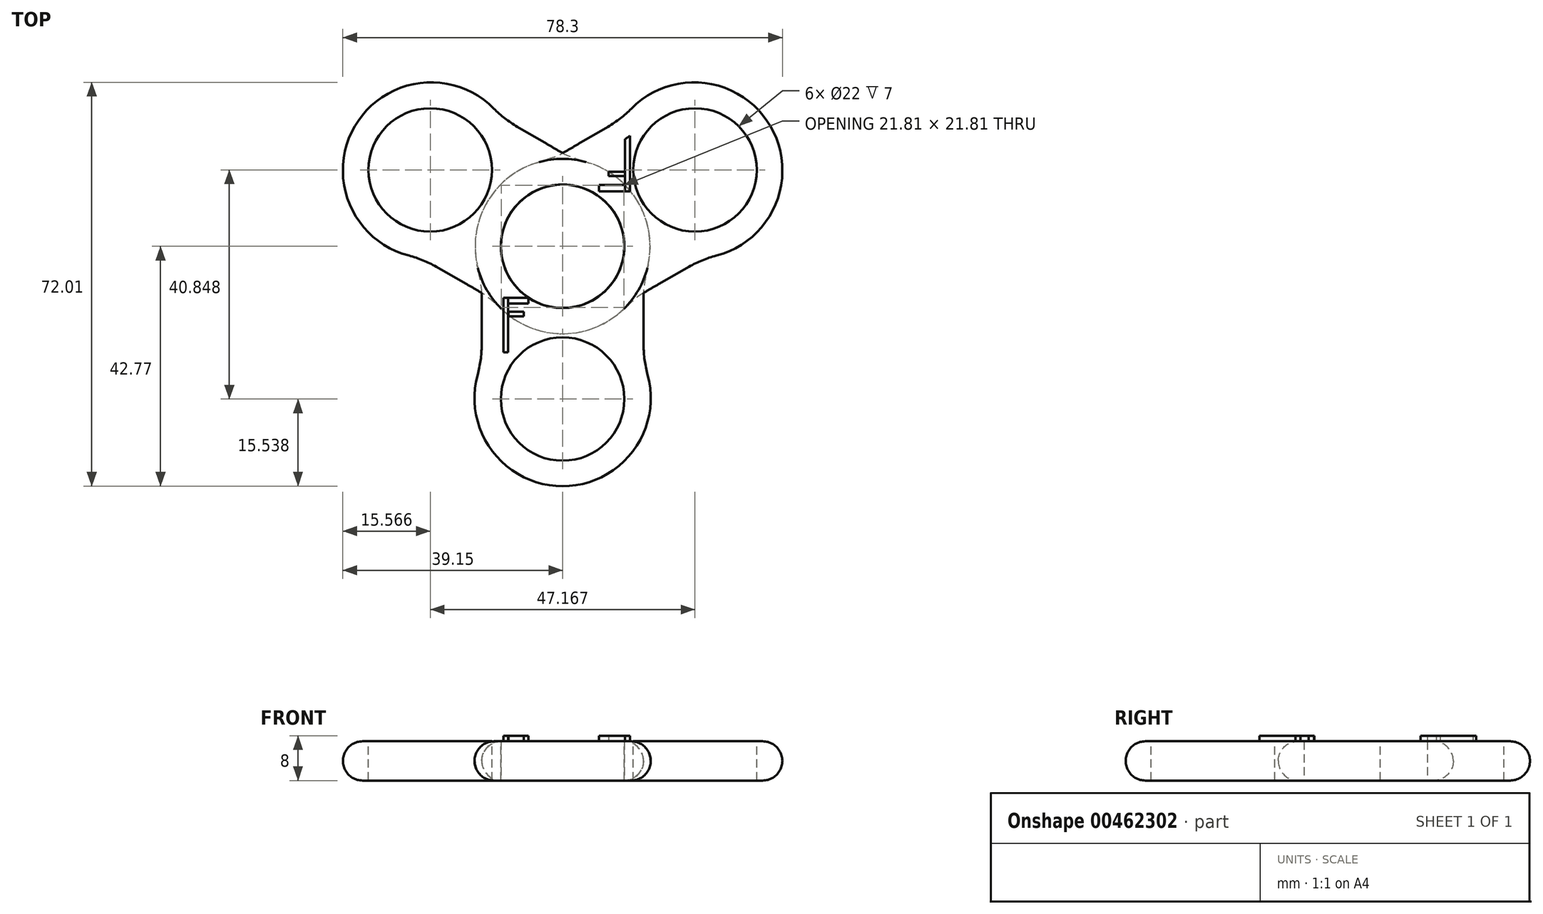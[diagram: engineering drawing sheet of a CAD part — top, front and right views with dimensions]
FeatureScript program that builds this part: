
annotation { "Feature Type Name" : "Feature", "Feature Type Description" : "" }
export const myFeature = defineFeature(function(context is Context, id is Id, definition is map)
    precondition{}
    {
        {
            var Q0;
            Q0=qCreatedBy(makeId("Top.planeOp"),FACE);
            var sketch = newSketch(context, id + "F0", { "sketchPlane" : qUnion([Q0])});
            skCircle(sketch, "E0", {"center": v(0, 0) * mm, "radius": 12.05 * mm});
            skSolve(sketch);
        }
        {
            var Q0;
            Q0=qCreatedBy(makeId("Top.planeOp"),FACE);
            var sketch = newSketch(context, id + "F1", { "sketchPlane" : qUnion([Q0])});
            skCircle(sketch, "E1", {"center": v(0, 0) * mm, "radius": 15.6 * mm});
            skSolve(sketch);
        }
        {
            var Q0;
            Q0=makeQuery(id+"F1.imprint","IMPRINT",FACE,{"disambiguationData":[TD([[makeQuery(id+"F1.imprint","IMPRINT",EDGE,{"derivedFrom":sQuery(id+"F1.wireOp",EDGE,"E1")}),1.0]])]});
            extrude(context, id + "F2", {"entities" : qUnion([Q0]), "depth" : 7 * mm, "offsetDistance" : 25 * mm});
        }
        {
            var Q0;
            Q0=sQuery(id+"F0.wireOp",VERTEX,"E0.center");
            var Q1;
            Q1=makeQuery(id+"F2.opExtrude","SWEPT_BODY",BODY,{"disambiguationData":[OSD([sQuery(id+"F1.wireOp",EDGE,"E1")])]});
            hole(context, id + "F3", {"style" : HoleStyle.SIMPLE, "endStyle" : HoleEndStyle.THROUGH, "oppositeDirection" : true, "holeDiameter" : 22 * mm, "majorDiameter" : 5 * mm, "isTappedThrough" : true, "tappedDepth" : 12 * mm, "tapClearance" : 3, "locations" : qUnion([Q0]), "scope" : qUnion([Q1])});
        }
        {
            var Q0;
            Q0=qCreatedBy(makeId("Top.planeOp"),FACE);
            var sketch = newSketch(context, id + "F4", { "sketchPlane" : qUnion([Q0])});
            skCircle(sketch, "E2", {"center": v(0, -27.23) * mm, "radius": 14.56 * mm});
            skSolve(sketch);
        }
        {
            var Q0;
            Q0=makeQuery(id+"F4.imprint","IMPRINT",FACE,{"disambiguationData":[TD([[makeQuery(id+"F4.imprint","IMPRINT",EDGE,{"derivedFrom":sQuery(id+"F4.wireOp",EDGE,"E2")}),1.0]])]});
            extrude(context, id + "F5", {"entities" : qUnion([Q0]), "operationType" : NewBodyOperationType.ADD, "depth" : 7 * mm, "offsetDistance" : 25 * mm});
        }
        {
            var Q0;
            Q0=makeQuery(id+"F5.boolean.opBoolean","MERGE",FACE,{"derivedFrom":[makeQuery(id+"F2.opExtrude","CAP_FACE",FACE,{"disambiguationData":[OSD([sQuery(id+"F1.wireOp",EDGE,"E1")])],"isStart":false}),makeQuery(id+"F5.opExtrude","CAP_FACE",FACE,{"disambiguationData":[OSD([sQuery(id+"F4.wireOp",EDGE,"E2")])],"isStart":false})]});
            var sketch = newSketch(context, id + "F6", { "sketchPlane" : qUnion([Q0])});
            skCircle(sketch, "E3", {"center": v(0, -27.23) * mm, "radius": 12.26 * mm});
            skSolve(sketch);
        }
        {
            var Q0;
            Q0=qCreatedBy(makeId("Top.planeOp"),FACE);
            var sketch = newSketch(context, id + "F7", { "sketchPlane" : qUnion([Q0])});
            skCircle(sketch, "E4", {"center": v(0, -27.07) * mm, "radius": 15.7 * mm});
            skSolve(sketch);
        }
        {
            var Q0;
            Q0=makeQuery(id+"F7.imprint","IMPRINT",FACE,{"disambiguationData":[TD([[makeQuery(id+"F7.imprint","IMPRINT",EDGE,{"derivedFrom":sQuery(id+"F7.wireOp",EDGE,"E4")}),1.0]])]});
            extrude(context, id + "F8", {"entities" : qUnion([Q0]), "operationType" : NewBodyOperationType.ADD, "depth" : 7 * mm, "offsetDistance" : 25 * mm});
        }
        {
            var Q0;
            Q0=sQuery(id+"F6.wireOp",VERTEX,"E3.center");
            var Q1;
            Q1=makeQuery(id+"F2.opExtrude","SWEPT_BODY",BODY,{"disambiguationData":[OSD([sQuery(id+"F1.wireOp",EDGE,"E1")])]});
            hole(context, id + "F9", {"style" : HoleStyle.SIMPLE, "endStyle" : HoleEndStyle.THROUGH, "holeDiameter" : 22 * mm, "majorDiameter" : 5 * mm, "isTappedThrough" : true, "tappedDepth" : 12 * mm, "tapClearance" : 3, "locations" : qUnion([Q0]), "scope" : qUnion([Q1])});
        }
        {
            var Q0;
            Q0=makeQuery(id+"F2.opExtrude","SWEPT_BODY",BODY,{"disambiguationData":[OSD([sQuery(id+"F1.wireOp",EDGE,"E1")])]});
            var Q1;
            Q1=makeQuery(id+"F2.opExtrude","SWEPT_FACE",FACE,{"disambiguationData":[OSD([sQuery(id+"F1.wireOp",EDGE,"E1")])]});
            circularPattern(context, id + "F10", {"entities" : qUnion([Q0]), "axis" : qUnion([Q1]), "angle" : 360 * degree, "instanceCount" : 3, "equalSpace" : true});
        }
        {
            var Q0;
            Q0=makeQuery(id+"F10.opPattern","COPY",EDGE,{"derivedFrom":makeQuery(id+"F8.boolean.opBoolean","INTERSECT",EDGE,{"disambiguationData":[OD(0.0)],"derivedFrom":[makeQuery(id+"F2.opExtrude","SWEPT_FACE",FACE,{"disambiguationData":[OSD([sQuery(id+"F1.wireOp",EDGE,"E1")])]}),makeQuery(id+"F8.opExtrude","SWEPT_FACE",FACE,{"disambiguationData":[OSD([sQuery(id+"F7.wireOp",EDGE,"E4")])]})]}),"instanceName":"2"});
            var Q1;
            Q1=makeQuery(id+"F8.boolean.opBoolean","INTERSECT",EDGE,{"disambiguationData":[OD(1.0)],"derivedFrom":[makeQuery(id+"F2.opExtrude","SWEPT_FACE",FACE,{"disambiguationData":[OSD([sQuery(id+"F1.wireOp",EDGE,"E1")])]}),makeQuery(id+"F8.opExtrude","SWEPT_FACE",FACE,{"disambiguationData":[OSD([sQuery(id+"F7.wireOp",EDGE,"E4")])]})]});
            var Q2;
            Q2=makeQuery(id+"F8.boolean.opBoolean","INTERSECT",EDGE,{"disambiguationData":[OD(0.0)],"derivedFrom":[makeQuery(id+"F2.opExtrude","SWEPT_FACE",FACE,{"disambiguationData":[OSD([sQuery(id+"F1.wireOp",EDGE,"E1")])]}),makeQuery(id+"F8.opExtrude","SWEPT_FACE",FACE,{"disambiguationData":[OSD([sQuery(id+"F7.wireOp",EDGE,"E4")])]})]});
            var Q3;
            Q3=makeQuery(id+"F10.opPattern","COPY",EDGE,{"derivedFrom":makeQuery(id+"F8.boolean.opBoolean","INTERSECT",EDGE,{"disambiguationData":[OD(1.0)],"derivedFrom":[makeQuery(id+"F2.opExtrude","SWEPT_FACE",FACE,{"disambiguationData":[OSD([sQuery(id+"F1.wireOp",EDGE,"E1")])]}),makeQuery(id+"F8.opExtrude","SWEPT_FACE",FACE,{"disambiguationData":[OSD([sQuery(id+"F7.wireOp",EDGE,"E4")])]})]}),"instanceName":"1"});
            var Q4;
            Q4=makeQuery(id+"F10.opPattern","COPY",EDGE,{"derivedFrom":makeQuery(id+"F8.boolean.opBoolean","INTERSECT",EDGE,{"disambiguationData":[OD(0.0)],"derivedFrom":[makeQuery(id+"F2.opExtrude","SWEPT_FACE",FACE,{"disambiguationData":[OSD([sQuery(id+"F1.wireOp",EDGE,"E1")])]}),makeQuery(id+"F8.opExtrude","SWEPT_FACE",FACE,{"disambiguationData":[OSD([sQuery(id+"F7.wireOp",EDGE,"E4")])]})]}),"instanceName":"1"});
            var Q5;
            Q5=makeQuery(id+"F10.opPattern","COPY",EDGE,{"derivedFrom":makeQuery(id+"F8.boolean.opBoolean","INTERSECT",EDGE,{"disambiguationData":[OD(1.0)],"derivedFrom":[makeQuery(id+"F2.opExtrude","SWEPT_FACE",FACE,{"disambiguationData":[OSD([sQuery(id+"F1.wireOp",EDGE,"E1")])]}),makeQuery(id+"F8.opExtrude","SWEPT_FACE",FACE,{"disambiguationData":[OSD([sQuery(id+"F7.wireOp",EDGE,"E4")])]})]}),"instanceName":"2"});
            chamfer(context, id + "F11", {"entities" : qUnion([Q0, Q1, Q2, Q3, Q4, Q5]), "width" : 19 * mm, "tangentPropagation" : true});
        }
        {
            var Q0;
            {var subQ0=makeQuery(id+"F2.opExtrude","SWEPT_FACE",FACE,{"disambiguationData":[OSD([sQuery(id+"F1.wireOp",EDGE,"E1")])]});Q0=makeQuery(id+"F11.opChamfer","BLEND_EDGE",EDGE,{"blendedFrom":[makeQuery(id+"F8.boolean.opBoolean","INTERSECT",EDGE,{"disambiguationData":[OD(1.0)],"derivedFrom":[subQ0,makeQuery(id+"F8.opExtrude","SWEPT_FACE",FACE,{"disambiguationData":[OSD([sQuery(id+"F7.wireOp",EDGE,"E4")])]})]}),subQ0],"blendedInto":[subQ0]});}
            var Q1;
            {var subQ0=makeQuery(id+"F2.opExtrude","SWEPT_FACE",FACE,{"disambiguationData":[OSD([sQuery(id+"F1.wireOp",EDGE,"E1")])]});Q1=makeQuery(id+"F11.opChamfer","BLEND_EDGE",EDGE,{"blendedFrom":[makeQuery(id+"F10.opPattern","COPY",EDGE,{"derivedFrom":makeQuery(id+"F8.boolean.opBoolean","INTERSECT",EDGE,{"disambiguationData":[OD(0.0)],"derivedFrom":[subQ0,makeQuery(id+"F8.opExtrude","SWEPT_FACE",FACE,{"disambiguationData":[OSD([sQuery(id+"F7.wireOp",EDGE,"E4")])]})]}),"instanceName":"2"}),makeQuery(id+"F10.opPattern","COPY",FACE,{"derivedFrom":subQ0,"instanceName":"2"})],"blendedInto":[makeQuery(id+"F10.opPattern","COPY",FACE,{"derivedFrom":subQ0,"instanceName":"2"})]});}
            var Q2;
            {var subQ0=makeQuery(id+"F2.opExtrude","SWEPT_FACE",FACE,{"disambiguationData":[OSD([sQuery(id+"F1.wireOp",EDGE,"E1")])]});Q2=makeQuery(id+"F11.opChamfer","BLEND_EDGE",EDGE,{"blendedFrom":[makeQuery(id+"F10.opPattern","COPY",EDGE,{"derivedFrom":makeQuery(id+"F8.boolean.opBoolean","INTERSECT",EDGE,{"disambiguationData":[OD(1.0)],"derivedFrom":[subQ0,makeQuery(id+"F8.opExtrude","SWEPT_FACE",FACE,{"disambiguationData":[OSD([sQuery(id+"F7.wireOp",EDGE,"E4")])]})]}),"instanceName":"2"}),makeQuery(id+"F10.opPattern","COPY",FACE,{"derivedFrom":subQ0,"instanceName":"2"})],"blendedInto":[makeQuery(id+"F10.opPattern","COPY",FACE,{"derivedFrom":subQ0,"instanceName":"2"})]});}
            var Q3;
            {var subQ0=makeQuery(id+"F2.opExtrude","SWEPT_FACE",FACE,{"disambiguationData":[OSD([sQuery(id+"F1.wireOp",EDGE,"E1")])]});Q3=makeQuery(id+"F11.opChamfer","BLEND_EDGE",EDGE,{"blendedFrom":[makeQuery(id+"F10.opPattern","COPY",EDGE,{"derivedFrom":makeQuery(id+"F8.boolean.opBoolean","INTERSECT",EDGE,{"disambiguationData":[OD(0.0)],"derivedFrom":[subQ0,makeQuery(id+"F8.opExtrude","SWEPT_FACE",FACE,{"disambiguationData":[OSD([sQuery(id+"F7.wireOp",EDGE,"E4")])]})]}),"instanceName":"1"}),makeQuery(id+"F10.opPattern","COPY",FACE,{"derivedFrom":subQ0,"instanceName":"1"})],"blendedInto":[makeQuery(id+"F10.opPattern","COPY",FACE,{"derivedFrom":subQ0,"instanceName":"1"})]});}
            var Q4;
            {var subQ0=makeQuery(id+"F2.opExtrude","SWEPT_FACE",FACE,{"disambiguationData":[OSD([sQuery(id+"F1.wireOp",EDGE,"E1")])]});Q4=makeQuery(id+"F11.opChamfer","BLEND_EDGE",EDGE,{"blendedFrom":[makeQuery(id+"F8.boolean.opBoolean","INTERSECT",EDGE,{"disambiguationData":[OD(0.0)],"derivedFrom":[subQ0,makeQuery(id+"F8.opExtrude","SWEPT_FACE",FACE,{"disambiguationData":[OSD([sQuery(id+"F7.wireOp",EDGE,"E4")])]})]}),subQ0],"blendedInto":[subQ0]});}
            var Q5;
            {var subQ0=makeQuery(id+"F2.opExtrude","SWEPT_FACE",FACE,{"disambiguationData":[OSD([sQuery(id+"F1.wireOp",EDGE,"E1")])]});Q5=makeQuery(id+"F11.opChamfer","BLEND_EDGE",EDGE,{"blendedFrom":[makeQuery(id+"F10.opPattern","COPY",EDGE,{"derivedFrom":makeQuery(id+"F8.boolean.opBoolean","INTERSECT",EDGE,{"disambiguationData":[OD(1.0)],"derivedFrom":[subQ0,makeQuery(id+"F8.opExtrude","SWEPT_FACE",FACE,{"disambiguationData":[OSD([sQuery(id+"F7.wireOp",EDGE,"E4")])]})]}),"instanceName":"1"}),makeQuery(id+"F10.opPattern","COPY",FACE,{"derivedFrom":subQ0,"instanceName":"1"})],"blendedInto":[makeQuery(id+"F10.opPattern","COPY",FACE,{"derivedFrom":subQ0,"instanceName":"1"})]});}
            fillet(context, id + "F12", {"entities" : qUnion([Q0, Q1, Q2, Q3, Q4, Q5]), "radius" : 40 * mm, "tangentPropagation" : true, "rho" : .8, "crossSection" : FilletCrossSection.CONIC, "allowEdgeOverflow" : false});
        }
        {
            var Q0;
            {var subQ0=makeQuery(id+"F8.opExtrude","SWEPT_FACE",FACE,{"disambiguationData":[OSD([sQuery(id+"F7.wireOp",EDGE,"E4")])]});Q0=makeQuery(id+"F11.opChamfer","BLEND_EDGE",EDGE,{"blendedFrom":[makeQuery(id+"F10.opPattern","COPY",EDGE,{"derivedFrom":makeQuery(id+"F8.boolean.opBoolean","INTERSECT",EDGE,{"disambiguationData":[OD(0.0)],"derivedFrom":[makeQuery(id+"F2.opExtrude","SWEPT_FACE",FACE,{"disambiguationData":[OSD([sQuery(id+"F1.wireOp",EDGE,"E1")])]}),subQ0]}),"instanceName":"1"}),makeQuery(id+"F10.opPattern","COPY",FACE,{"derivedFrom":subQ0,"instanceName":"1"})],"blendedInto":[makeQuery(id+"F10.opPattern","COPY",FACE,{"derivedFrom":subQ0,"instanceName":"1"})]});}
            var Q1;
            {var subQ0=makeQuery(id+"F8.opExtrude","SWEPT_FACE",FACE,{"disambiguationData":[OSD([sQuery(id+"F7.wireOp",EDGE,"E4")])]});Q1=makeQuery(id+"F11.opChamfer","BLEND_EDGE",EDGE,{"blendedFrom":[makeQuery(id+"F10.opPattern","COPY",EDGE,{"derivedFrom":makeQuery(id+"F8.boolean.opBoolean","INTERSECT",EDGE,{"disambiguationData":[OD(1.0)],"derivedFrom":[makeQuery(id+"F2.opExtrude","SWEPT_FACE",FACE,{"disambiguationData":[OSD([sQuery(id+"F1.wireOp",EDGE,"E1")])]}),subQ0]}),"instanceName":"1"}),makeQuery(id+"F10.opPattern","COPY",FACE,{"derivedFrom":subQ0,"instanceName":"1"})],"blendedInto":[makeQuery(id+"F10.opPattern","COPY",FACE,{"derivedFrom":subQ0,"instanceName":"1"})]});}
            var Q2;
            {var subQ0=makeQuery(id+"F8.opExtrude","SWEPT_FACE",FACE,{"disambiguationData":[OSD([sQuery(id+"F7.wireOp",EDGE,"E4")])]});Q2=makeQuery(id+"F11.opChamfer","BLEND_EDGE",EDGE,{"blendedFrom":[makeQuery(id+"F8.boolean.opBoolean","INTERSECT",EDGE,{"disambiguationData":[OD(0.0)],"derivedFrom":[makeQuery(id+"F2.opExtrude","SWEPT_FACE",FACE,{"disambiguationData":[OSD([sQuery(id+"F1.wireOp",EDGE,"E1")])]}),subQ0]}),subQ0],"blendedInto":[subQ0]});}
            var Q3;
            {var subQ0=makeQuery(id+"F8.opExtrude","SWEPT_FACE",FACE,{"disambiguationData":[OSD([sQuery(id+"F7.wireOp",EDGE,"E4")])]});Q3=makeQuery(id+"F11.opChamfer","BLEND_EDGE",EDGE,{"blendedFrom":[makeQuery(id+"F10.opPattern","COPY",EDGE,{"derivedFrom":makeQuery(id+"F8.boolean.opBoolean","INTERSECT",EDGE,{"disambiguationData":[OD(1.0)],"derivedFrom":[makeQuery(id+"F2.opExtrude","SWEPT_FACE",FACE,{"disambiguationData":[OSD([sQuery(id+"F1.wireOp",EDGE,"E1")])]}),subQ0]}),"instanceName":"2"}),makeQuery(id+"F10.opPattern","COPY",FACE,{"derivedFrom":subQ0,"instanceName":"2"})],"blendedInto":[makeQuery(id+"F10.opPattern","COPY",FACE,{"derivedFrom":subQ0,"instanceName":"2"})]});}
            var Q4;
            {var subQ0=makeQuery(id+"F8.opExtrude","SWEPT_FACE",FACE,{"disambiguationData":[OSD([sQuery(id+"F7.wireOp",EDGE,"E4")])]});Q4=makeQuery(id+"F11.opChamfer","BLEND_EDGE",EDGE,{"blendedFrom":[makeQuery(id+"F8.boolean.opBoolean","INTERSECT",EDGE,{"disambiguationData":[OD(1.0)],"derivedFrom":[makeQuery(id+"F2.opExtrude","SWEPT_FACE",FACE,{"disambiguationData":[OSD([sQuery(id+"F1.wireOp",EDGE,"E1")])]}),subQ0]}),subQ0],"blendedInto":[subQ0]});}
            var Q5;
            {var subQ0=makeQuery(id+"F8.opExtrude","SWEPT_FACE",FACE,{"disambiguationData":[OSD([sQuery(id+"F7.wireOp",EDGE,"E4")])]});Q5=makeQuery(id+"F11.opChamfer","BLEND_EDGE",EDGE,{"blendedFrom":[makeQuery(id+"F10.opPattern","COPY",EDGE,{"derivedFrom":makeQuery(id+"F8.boolean.opBoolean","INTERSECT",EDGE,{"disambiguationData":[OD(0.0)],"derivedFrom":[makeQuery(id+"F2.opExtrude","SWEPT_FACE",FACE,{"disambiguationData":[OSD([sQuery(id+"F1.wireOp",EDGE,"E1")])]}),subQ0]}),"instanceName":"2"}),makeQuery(id+"F10.opPattern","COPY",FACE,{"derivedFrom":subQ0,"instanceName":"2"})],"blendedInto":[makeQuery(id+"F10.opPattern","COPY",FACE,{"derivedFrom":subQ0,"instanceName":"2"})]});}
            fillet(context, id + "F13", {"entities" : qUnion([Q0, Q1, Q2, Q3, Q4, Q5]), "radius" : 20 * mm, "tangentPropagation" : true, "allowEdgeOverflow" : false});
        }
        {
            var Q0;
            {var subQ0=sQuery(id+"F7.wireOp",EDGE,"E4");var subQ1=sQuery(id+"F1.wireOp",EDGE,"E1");var subQ2=makeQuery(id+"F2.opExtrude","SWEPT_FACE",FACE,{"disambiguationData":[OSD([subQ1])]});Q0=makeQuery(id+"F12.opFillet","BLEND_EDGE",EDGE,{"blendedFrom":[makeQuery(id+"F11.opChamfer","BLEND_EDGE",EDGE,{"blendedFrom":[makeQuery(id+"F10.opPattern","COPY",EDGE,{"derivedFrom":makeQuery(id+"F8.boolean.opBoolean","INTERSECT",EDGE,{"disambiguationData":[OD(0.0)],"derivedFrom":[subQ2,makeQuery(id+"F8.opExtrude","SWEPT_FACE",FACE,{"disambiguationData":[OSD([subQ0])]})]}),"instanceName":"1"}),makeQuery(id+"F10.opPattern","COPY",FACE,{"derivedFrom":subQ2,"instanceName":"1"})],"blendedInto":[makeQuery(id+"F10.opPattern","COPY",FACE,{"derivedFrom":subQ2,"instanceName":"1"})]}),makeQuery(id+"F10.opPattern","COPY",FACE,{"derivedFrom":makeQuery(id+"F8.boolean.opBoolean","MERGE",FACE,{"derivedFrom":[makeQuery(id+"F5.boolean.opBoolean","MERGE",FACE,{"derivedFrom":[makeQuery(id+"F2.opExtrude","CAP_FACE",FACE,{"disambiguationData":[OSD([subQ1])],"isStart":false}),makeQuery(id+"F5.opExtrude","CAP_FACE",FACE,{"disambiguationData":[OSD([sQuery(id+"F4.wireOp",EDGE,"E2")])],"isStart":false})]}),makeQuery(id+"F8.opExtrude","CAP_FACE",FACE,{"disambiguationData":[OSD([subQ0])],"isStart":false})]}),"instanceName":"1"})],"blendedInto":[makeQuery(id+"F10.opPattern","COPY",FACE,{"derivedFrom":makeQuery(id+"F8.boolean.opBoolean","MERGE",FACE,{"derivedFrom":[makeQuery(id+"F5.boolean.opBoolean","MERGE",FACE,{"derivedFrom":[makeQuery(id+"F2.opExtrude","CAP_FACE",FACE,{"disambiguationData":[OSD([subQ1])],"isStart":false}),makeQuery(id+"F5.opExtrude","CAP_FACE",FACE,{"disambiguationData":[OSD([sQuery(id+"F4.wireOp",EDGE,"E2")])],"isStart":false})]}),makeQuery(id+"F8.opExtrude","CAP_FACE",FACE,{"disambiguationData":[OSD([subQ0])],"isStart":false})]}),"instanceName":"1"})]});}
            var Q1;
            {var subQ0=sQuery(id+"F7.wireOp",EDGE,"E4");var subQ1=sQuery(id+"F1.wireOp",EDGE,"E1");var subQ2=makeQuery(id+"F2.opExtrude","SWEPT_FACE",FACE,{"disambiguationData":[OSD([subQ1])]});Q1=makeQuery(id+"F12.opFillet","BLEND_EDGE",EDGE,{"blendedFrom":[makeQuery(id+"F11.opChamfer","BLEND_EDGE",EDGE,{"blendedFrom":[makeQuery(id+"F10.opPattern","COPY",EDGE,{"derivedFrom":makeQuery(id+"F8.boolean.opBoolean","INTERSECT",EDGE,{"disambiguationData":[OD(0.0)],"derivedFrom":[subQ2,makeQuery(id+"F8.opExtrude","SWEPT_FACE",FACE,{"disambiguationData":[OSD([subQ0])]})]}),"instanceName":"2"}),makeQuery(id+"F10.opPattern","COPY",FACE,{"derivedFrom":subQ2,"instanceName":"2"})],"blendedInto":[makeQuery(id+"F10.opPattern","COPY",FACE,{"derivedFrom":subQ2,"instanceName":"2"})]}),makeQuery(id+"F10.opPattern","COPY",FACE,{"derivedFrom":makeQuery(id+"F8.boolean.opBoolean","MERGE",FACE,{"derivedFrom":[makeQuery(id+"F5.boolean.opBoolean","MERGE",FACE,{"derivedFrom":[makeQuery(id+"F2.opExtrude","CAP_FACE",FACE,{"disambiguationData":[OSD([subQ1])],"isStart":false}),makeQuery(id+"F5.opExtrude","CAP_FACE",FACE,{"disambiguationData":[OSD([sQuery(id+"F4.wireOp",EDGE,"E2")])],"isStart":false})]}),makeQuery(id+"F8.opExtrude","CAP_FACE",FACE,{"disambiguationData":[OSD([subQ0])],"isStart":false})]}),"instanceName":"2"})],"blendedInto":[makeQuery(id+"F10.opPattern","COPY",FACE,{"derivedFrom":makeQuery(id+"F8.boolean.opBoolean","MERGE",FACE,{"derivedFrom":[makeQuery(id+"F5.boolean.opBoolean","MERGE",FACE,{"derivedFrom":[makeQuery(id+"F2.opExtrude","CAP_FACE",FACE,{"disambiguationData":[OSD([subQ1])],"isStart":false}),makeQuery(id+"F5.opExtrude","CAP_FACE",FACE,{"disambiguationData":[OSD([sQuery(id+"F4.wireOp",EDGE,"E2")])],"isStart":false})]}),makeQuery(id+"F8.opExtrude","CAP_FACE",FACE,{"disambiguationData":[OSD([subQ0])],"isStart":false})]}),"instanceName":"2"})]});}
            var Q2;
            {var subQ0=sQuery(id+"F7.wireOp",EDGE,"E4");var subQ1=sQuery(id+"F1.wireOp",EDGE,"E1");var subQ2=makeQuery(id+"F8.opExtrude","SWEPT_FACE",FACE,{"disambiguationData":[OSD([subQ0])]});Q2=makeQuery(id+"F13.opFillet","BLEND_EDGE",EDGE,{"blendedFrom":[makeQuery(id+"F11.opChamfer","BLEND_EDGE",EDGE,{"blendedFrom":[makeQuery(id+"F8.boolean.opBoolean","INTERSECT",EDGE,{"disambiguationData":[OD(1.0)],"derivedFrom":[makeQuery(id+"F2.opExtrude","SWEPT_FACE",FACE,{"disambiguationData":[OSD([subQ1])]}),subQ2]}),subQ2],"blendedInto":[subQ2]}),makeQuery(id+"F8.boolean.opBoolean","MERGE",FACE,{"derivedFrom":[makeQuery(id+"F5.boolean.opBoolean","MERGE",FACE,{"derivedFrom":[makeQuery(id+"F2.opExtrude","CAP_FACE",FACE,{"disambiguationData":[OSD([subQ1])],"isStart":false}),makeQuery(id+"F5.opExtrude","CAP_FACE",FACE,{"disambiguationData":[OSD([sQuery(id+"F4.wireOp",EDGE,"E2")])],"isStart":false})]}),makeQuery(id+"F8.opExtrude","CAP_FACE",FACE,{"disambiguationData":[OSD([subQ0])],"isStart":false})]})],"blendedInto":[makeQuery(id+"F8.boolean.opBoolean","MERGE",FACE,{"derivedFrom":[makeQuery(id+"F5.boolean.opBoolean","MERGE",FACE,{"derivedFrom":[makeQuery(id+"F2.opExtrude","CAP_FACE",FACE,{"disambiguationData":[OSD([subQ1])],"isStart":false}),makeQuery(id+"F5.opExtrude","CAP_FACE",FACE,{"disambiguationData":[OSD([sQuery(id+"F4.wireOp",EDGE,"E2")])],"isStart":false})]}),makeQuery(id+"F8.opExtrude","CAP_FACE",FACE,{"disambiguationData":[OSD([subQ0])],"isStart":false})]})]});}
            var Q3;
            {var subQ0=sQuery(id+"F7.wireOp",EDGE,"E4");var subQ1=sQuery(id+"F1.wireOp",EDGE,"E1");var subQ2=makeQuery(id+"F2.opExtrude","SWEPT_FACE",FACE,{"disambiguationData":[OSD([subQ1])]});Q3=makeQuery(id+"F12.opFillet","BLEND_EDGE",EDGE,{"blendedFrom":[makeQuery(id+"F11.opChamfer","BLEND_EDGE",EDGE,{"blendedFrom":[makeQuery(id+"F8.boolean.opBoolean","INTERSECT",EDGE,{"disambiguationData":[OD(0.0)],"derivedFrom":[subQ2,makeQuery(id+"F8.opExtrude","SWEPT_FACE",FACE,{"disambiguationData":[OSD([subQ0])]})]}),subQ2],"blendedInto":[subQ2]}),makeQuery(id+"F8.boolean.opBoolean","MERGE",FACE,{"derivedFrom":[makeQuery(id+"F5.boolean.opBoolean","MERGE",FACE,{"derivedFrom":[makeQuery(id+"F2.opExtrude","CAP_FACE",FACE,{"disambiguationData":[OSD([subQ1])],"isStart":false}),makeQuery(id+"F5.opExtrude","CAP_FACE",FACE,{"disambiguationData":[OSD([sQuery(id+"F4.wireOp",EDGE,"E2")])],"isStart":false})]}),makeQuery(id+"F8.opExtrude","CAP_FACE",FACE,{"disambiguationData":[OSD([subQ0])],"isStart":false})]})],"blendedInto":[makeQuery(id+"F8.boolean.opBoolean","MERGE",FACE,{"derivedFrom":[makeQuery(id+"F5.boolean.opBoolean","MERGE",FACE,{"derivedFrom":[makeQuery(id+"F2.opExtrude","CAP_FACE",FACE,{"disambiguationData":[OSD([subQ1])],"isStart":false}),makeQuery(id+"F5.opExtrude","CAP_FACE",FACE,{"disambiguationData":[OSD([sQuery(id+"F4.wireOp",EDGE,"E2")])],"isStart":false})]}),makeQuery(id+"F8.opExtrude","CAP_FACE",FACE,{"disambiguationData":[OSD([subQ0])],"isStart":false})]})]});}
            var Q4;
            {var subQ0=sQuery(id+"F7.wireOp",EDGE,"E4");var subQ1=sQuery(id+"F1.wireOp",EDGE,"E1");var subQ2=makeQuery(id+"F2.opExtrude","SWEPT_FACE",FACE,{"disambiguationData":[OSD([subQ1])]});Q4=makeQuery(id+"F12.opFillet","BLEND_EDGE",EDGE,{"blendedFrom":[makeQuery(id+"F11.opChamfer","BLEND_EDGE",EDGE,{"blendedFrom":[makeQuery(id+"F8.boolean.opBoolean","INTERSECT",EDGE,{"disambiguationData":[OD(1.0)],"derivedFrom":[subQ2,makeQuery(id+"F8.opExtrude","SWEPT_FACE",FACE,{"disambiguationData":[OSD([subQ0])]})]}),subQ2],"blendedInto":[subQ2]}),makeQuery(id+"F8.boolean.opBoolean","MERGE",FACE,{"derivedFrom":[makeQuery(id+"F5.boolean.opBoolean","MERGE",FACE,{"derivedFrom":[makeQuery(id+"F2.opExtrude","CAP_FACE",FACE,{"disambiguationData":[OSD([subQ1])],"isStart":false}),makeQuery(id+"F5.opExtrude","CAP_FACE",FACE,{"disambiguationData":[OSD([sQuery(id+"F4.wireOp",EDGE,"E2")])],"isStart":false})]}),makeQuery(id+"F8.opExtrude","CAP_FACE",FACE,{"disambiguationData":[OSD([subQ0])],"isStart":false})]})],"blendedInto":[makeQuery(id+"F8.boolean.opBoolean","MERGE",FACE,{"derivedFrom":[makeQuery(id+"F5.boolean.opBoolean","MERGE",FACE,{"derivedFrom":[makeQuery(id+"F2.opExtrude","CAP_FACE",FACE,{"disambiguationData":[OSD([subQ1])],"isStart":false}),makeQuery(id+"F5.opExtrude","CAP_FACE",FACE,{"disambiguationData":[OSD([sQuery(id+"F4.wireOp",EDGE,"E2")])],"isStart":false})]}),makeQuery(id+"F8.opExtrude","CAP_FACE",FACE,{"disambiguationData":[OSD([subQ0])],"isStart":false})]})]});}
            var Q5;
            Q5=makeQuery(id+"F8.opExtrude","CAP_EDGE",EDGE,{"disambiguationData":[OSD([sQuery(id+"F7.wireOp",EDGE,"E4")])],"isStart":false});
            var Q6;
            {var subQ0=sQuery(id+"F7.wireOp",EDGE,"E4");var subQ1=sQuery(id+"F1.wireOp",EDGE,"E1");var subQ2=makeQuery(id+"F2.opExtrude","SWEPT_FACE",FACE,{"disambiguationData":[OSD([subQ1])]});Q6=makeQuery(id+"F12.opFillet","BLEND_EDGE",EDGE,{"blendedFrom":[makeQuery(id+"F11.opChamfer","BLEND_EDGE",EDGE,{"blendedFrom":[makeQuery(id+"F10.opPattern","COPY",EDGE,{"derivedFrom":makeQuery(id+"F8.boolean.opBoolean","INTERSECT",EDGE,{"disambiguationData":[OD(1.0)],"derivedFrom":[subQ2,makeQuery(id+"F8.opExtrude","SWEPT_FACE",FACE,{"disambiguationData":[OSD([subQ0])]})]}),"instanceName":"2"}),makeQuery(id+"F10.opPattern","COPY",FACE,{"derivedFrom":subQ2,"instanceName":"2"})],"blendedInto":[makeQuery(id+"F10.opPattern","COPY",FACE,{"derivedFrom":subQ2,"instanceName":"2"})]}),makeQuery(id+"F10.opPattern","COPY",FACE,{"derivedFrom":makeQuery(id+"F8.boolean.opBoolean","MERGE",FACE,{"derivedFrom":[makeQuery(id+"F5.boolean.opBoolean","MERGE",FACE,{"derivedFrom":[makeQuery(id+"F2.opExtrude","CAP_FACE",FACE,{"disambiguationData":[OSD([subQ1])],"isStart":false}),makeQuery(id+"F5.opExtrude","CAP_FACE",FACE,{"disambiguationData":[OSD([sQuery(id+"F4.wireOp",EDGE,"E2")])],"isStart":false})]}),makeQuery(id+"F8.opExtrude","CAP_FACE",FACE,{"disambiguationData":[OSD([subQ0])],"isStart":false})]}),"instanceName":"2"})],"blendedInto":[makeQuery(id+"F10.opPattern","COPY",FACE,{"derivedFrom":makeQuery(id+"F8.boolean.opBoolean","MERGE",FACE,{"derivedFrom":[makeQuery(id+"F5.boolean.opBoolean","MERGE",FACE,{"derivedFrom":[makeQuery(id+"F2.opExtrude","CAP_FACE",FACE,{"disambiguationData":[OSD([subQ1])],"isStart":false}),makeQuery(id+"F5.opExtrude","CAP_FACE",FACE,{"disambiguationData":[OSD([sQuery(id+"F4.wireOp",EDGE,"E2")])],"isStart":false})]}),makeQuery(id+"F8.opExtrude","CAP_FACE",FACE,{"disambiguationData":[OSD([subQ0])],"isStart":false})]}),"instanceName":"2"})]});}
            var Q7;
            {var subQ0=sQuery(id+"F7.wireOp",EDGE,"E4");var subQ1=sQuery(id+"F1.wireOp",EDGE,"E1");var subQ2=makeQuery(id+"F8.opExtrude","SWEPT_FACE",FACE,{"disambiguationData":[OSD([subQ0])]});Q7=makeQuery(id+"F13.opFillet","BLEND_EDGE",EDGE,{"blendedFrom":[makeQuery(id+"F11.opChamfer","BLEND_EDGE",EDGE,{"blendedFrom":[makeQuery(id+"F10.opPattern","COPY",EDGE,{"derivedFrom":makeQuery(id+"F8.boolean.opBoolean","INTERSECT",EDGE,{"disambiguationData":[OD(1.0)],"derivedFrom":[makeQuery(id+"F2.opExtrude","SWEPT_FACE",FACE,{"disambiguationData":[OSD([subQ1])]}),subQ2]}),"instanceName":"2"}),makeQuery(id+"F10.opPattern","COPY",FACE,{"derivedFrom":subQ2,"instanceName":"2"})],"blendedInto":[makeQuery(id+"F10.opPattern","COPY",FACE,{"derivedFrom":subQ2,"instanceName":"2"})]}),makeQuery(id+"F10.opPattern","COPY",FACE,{"derivedFrom":makeQuery(id+"F8.boolean.opBoolean","MERGE",FACE,{"derivedFrom":[makeQuery(id+"F5.boolean.opBoolean","MERGE",FACE,{"derivedFrom":[makeQuery(id+"F2.opExtrude","CAP_FACE",FACE,{"disambiguationData":[OSD([subQ1])],"isStart":false}),makeQuery(id+"F5.opExtrude","CAP_FACE",FACE,{"disambiguationData":[OSD([sQuery(id+"F4.wireOp",EDGE,"E2")])],"isStart":false})]}),makeQuery(id+"F8.opExtrude","CAP_FACE",FACE,{"disambiguationData":[OSD([subQ0])],"isStart":false})]}),"instanceName":"2"})],"blendedInto":[makeQuery(id+"F10.opPattern","COPY",FACE,{"derivedFrom":makeQuery(id+"F8.boolean.opBoolean","MERGE",FACE,{"derivedFrom":[makeQuery(id+"F5.boolean.opBoolean","MERGE",FACE,{"derivedFrom":[makeQuery(id+"F2.opExtrude","CAP_FACE",FACE,{"disambiguationData":[OSD([subQ1])],"isStart":false}),makeQuery(id+"F5.opExtrude","CAP_FACE",FACE,{"disambiguationData":[OSD([sQuery(id+"F4.wireOp",EDGE,"E2")])],"isStart":false})]}),makeQuery(id+"F8.opExtrude","CAP_FACE",FACE,{"disambiguationData":[OSD([subQ0])],"isStart":false})]}),"instanceName":"2"})]});}
            var Q8;
            {var subQ0=sQuery(id+"F7.wireOp",EDGE,"E4");var subQ1=sQuery(id+"F1.wireOp",EDGE,"E1");var subQ2=makeQuery(id+"F8.opExtrude","SWEPT_FACE",FACE,{"disambiguationData":[OSD([subQ0])]});Q8=makeQuery(id+"F13.opFillet","BLEND_EDGE",EDGE,{"blendedFrom":[makeQuery(id+"F11.opChamfer","BLEND_EDGE",EDGE,{"blendedFrom":[makeQuery(id+"F10.opPattern","COPY",EDGE,{"derivedFrom":makeQuery(id+"F8.boolean.opBoolean","INTERSECT",EDGE,{"disambiguationData":[OD(1.0)],"derivedFrom":[makeQuery(id+"F2.opExtrude","SWEPT_FACE",FACE,{"disambiguationData":[OSD([subQ1])]}),subQ2]}),"instanceName":"1"}),makeQuery(id+"F10.opPattern","COPY",FACE,{"derivedFrom":subQ2,"instanceName":"1"})],"blendedInto":[makeQuery(id+"F10.opPattern","COPY",FACE,{"derivedFrom":subQ2,"instanceName":"1"})]}),makeQuery(id+"F10.opPattern","COPY",FACE,{"derivedFrom":makeQuery(id+"F8.boolean.opBoolean","MERGE",FACE,{"derivedFrom":[makeQuery(id+"F5.boolean.opBoolean","MERGE",FACE,{"derivedFrom":[makeQuery(id+"F2.opExtrude","CAP_FACE",FACE,{"disambiguationData":[OSD([subQ1])],"isStart":false}),makeQuery(id+"F5.opExtrude","CAP_FACE",FACE,{"disambiguationData":[OSD([sQuery(id+"F4.wireOp",EDGE,"E2")])],"isStart":false})]}),makeQuery(id+"F8.opExtrude","CAP_FACE",FACE,{"disambiguationData":[OSD([subQ0])],"isStart":false})]}),"instanceName":"1"})],"blendedInto":[makeQuery(id+"F10.opPattern","COPY",FACE,{"derivedFrom":makeQuery(id+"F8.boolean.opBoolean","MERGE",FACE,{"derivedFrom":[makeQuery(id+"F5.boolean.opBoolean","MERGE",FACE,{"derivedFrom":[makeQuery(id+"F2.opExtrude","CAP_FACE",FACE,{"disambiguationData":[OSD([subQ1])],"isStart":false}),makeQuery(id+"F5.opExtrude","CAP_FACE",FACE,{"disambiguationData":[OSD([sQuery(id+"F4.wireOp",EDGE,"E2")])],"isStart":false})]}),makeQuery(id+"F8.opExtrude","CAP_FACE",FACE,{"disambiguationData":[OSD([subQ0])],"isStart":false})]}),"instanceName":"1"})]});}
            var Q9;
            {var subQ0=sQuery(id+"F7.wireOp",EDGE,"E4");var subQ1=sQuery(id+"F1.wireOp",EDGE,"E1");var subQ2=makeQuery(id+"F8.opExtrude","SWEPT_FACE",FACE,{"disambiguationData":[OSD([subQ0])]});Q9=makeQuery(id+"F13.opFillet","BLEND_EDGE",EDGE,{"blendedFrom":[makeQuery(id+"F11.opChamfer","BLEND_EDGE",EDGE,{"blendedFrom":[makeQuery(id+"F10.opPattern","COPY",EDGE,{"derivedFrom":makeQuery(id+"F8.boolean.opBoolean","INTERSECT",EDGE,{"disambiguationData":[OD(0.0)],"derivedFrom":[makeQuery(id+"F2.opExtrude","SWEPT_FACE",FACE,{"disambiguationData":[OSD([subQ1])]}),subQ2]}),"instanceName":"1"}),makeQuery(id+"F10.opPattern","COPY",FACE,{"derivedFrom":subQ2,"instanceName":"1"})],"blendedInto":[makeQuery(id+"F10.opPattern","COPY",FACE,{"derivedFrom":subQ2,"instanceName":"1"})]}),makeQuery(id+"F10.opPattern","COPY",FACE,{"derivedFrom":makeQuery(id+"F8.boolean.opBoolean","MERGE",FACE,{"derivedFrom":[makeQuery(id+"F5.boolean.opBoolean","MERGE",FACE,{"derivedFrom":[makeQuery(id+"F2.opExtrude","CAP_FACE",FACE,{"disambiguationData":[OSD([subQ1])],"isStart":false}),makeQuery(id+"F5.opExtrude","CAP_FACE",FACE,{"disambiguationData":[OSD([sQuery(id+"F4.wireOp",EDGE,"E2")])],"isStart":false})]}),makeQuery(id+"F8.opExtrude","CAP_FACE",FACE,{"disambiguationData":[OSD([subQ0])],"isStart":false})]}),"instanceName":"1"})],"blendedInto":[makeQuery(id+"F10.opPattern","COPY",FACE,{"derivedFrom":makeQuery(id+"F8.boolean.opBoolean","MERGE",FACE,{"derivedFrom":[makeQuery(id+"F5.boolean.opBoolean","MERGE",FACE,{"derivedFrom":[makeQuery(id+"F2.opExtrude","CAP_FACE",FACE,{"disambiguationData":[OSD([subQ1])],"isStart":false}),makeQuery(id+"F5.opExtrude","CAP_FACE",FACE,{"disambiguationData":[OSD([sQuery(id+"F4.wireOp",EDGE,"E2")])],"isStart":false})]}),makeQuery(id+"F8.opExtrude","CAP_FACE",FACE,{"disambiguationData":[OSD([subQ0])],"isStart":false})]}),"instanceName":"1"})]});}
            var Q10;
            {var subQ0=sQuery(id+"F7.wireOp",EDGE,"E4");var subQ1=sQuery(id+"F1.wireOp",EDGE,"E1");var subQ2=makeQuery(id+"F8.opExtrude","SWEPT_FACE",FACE,{"disambiguationData":[OSD([subQ0])]});Q10=makeQuery(id+"F13.opFillet","BLEND_EDGE",EDGE,{"blendedFrom":[makeQuery(id+"F11.opChamfer","BLEND_EDGE",EDGE,{"blendedFrom":[makeQuery(id+"F8.boolean.opBoolean","INTERSECT",EDGE,{"disambiguationData":[OD(0.0)],"derivedFrom":[makeQuery(id+"F2.opExtrude","SWEPT_FACE",FACE,{"disambiguationData":[OSD([subQ1])]}),subQ2]}),subQ2],"blendedInto":[subQ2]}),makeQuery(id+"F8.boolean.opBoolean","MERGE",FACE,{"derivedFrom":[makeQuery(id+"F5.boolean.opBoolean","MERGE",FACE,{"derivedFrom":[makeQuery(id+"F2.opExtrude","CAP_FACE",FACE,{"disambiguationData":[OSD([subQ1])],"isStart":false}),makeQuery(id+"F5.opExtrude","CAP_FACE",FACE,{"disambiguationData":[OSD([sQuery(id+"F4.wireOp",EDGE,"E2")])],"isStart":false})]}),makeQuery(id+"F8.opExtrude","CAP_FACE",FACE,{"disambiguationData":[OSD([subQ0])],"isStart":false})]})],"blendedInto":[makeQuery(id+"F8.boolean.opBoolean","MERGE",FACE,{"derivedFrom":[makeQuery(id+"F5.boolean.opBoolean","MERGE",FACE,{"derivedFrom":[makeQuery(id+"F2.opExtrude","CAP_FACE",FACE,{"disambiguationData":[OSD([subQ1])],"isStart":false}),makeQuery(id+"F5.opExtrude","CAP_FACE",FACE,{"disambiguationData":[OSD([sQuery(id+"F4.wireOp",EDGE,"E2")])],"isStart":false})]}),makeQuery(id+"F8.opExtrude","CAP_FACE",FACE,{"disambiguationData":[OSD([subQ0])],"isStart":false})]})]});}
            var Q11;
            Q11=makeQuery(id+"F10.opPattern","COPY",EDGE,{"derivedFrom":makeQuery(id+"F8.opExtrude","CAP_EDGE",EDGE,{"disambiguationData":[OSD([sQuery(id+"F7.wireOp",EDGE,"E4")])],"isStart":false}),"instanceName":"2"});
            var Q12;
            {var subQ0=sQuery(id+"F7.wireOp",EDGE,"E4");var subQ1=sQuery(id+"F1.wireOp",EDGE,"E1");var subQ2=makeQuery(id+"F8.opExtrude","SWEPT_FACE",FACE,{"disambiguationData":[OSD([subQ0])]});Q12=makeQuery(id+"F13.opFillet","BLEND_EDGE",EDGE,{"blendedFrom":[makeQuery(id+"F11.opChamfer","BLEND_EDGE",EDGE,{"blendedFrom":[makeQuery(id+"F10.opPattern","COPY",EDGE,{"derivedFrom":makeQuery(id+"F8.boolean.opBoolean","INTERSECT",EDGE,{"disambiguationData":[OD(0.0)],"derivedFrom":[makeQuery(id+"F2.opExtrude","SWEPT_FACE",FACE,{"disambiguationData":[OSD([subQ1])]}),subQ2]}),"instanceName":"2"}),makeQuery(id+"F10.opPattern","COPY",FACE,{"derivedFrom":subQ2,"instanceName":"2"})],"blendedInto":[makeQuery(id+"F10.opPattern","COPY",FACE,{"derivedFrom":subQ2,"instanceName":"2"})]}),makeQuery(id+"F10.opPattern","COPY",FACE,{"derivedFrom":makeQuery(id+"F8.boolean.opBoolean","MERGE",FACE,{"derivedFrom":[makeQuery(id+"F5.boolean.opBoolean","MERGE",FACE,{"derivedFrom":[makeQuery(id+"F2.opExtrude","CAP_FACE",FACE,{"disambiguationData":[OSD([subQ1])],"isStart":false}),makeQuery(id+"F5.opExtrude","CAP_FACE",FACE,{"disambiguationData":[OSD([sQuery(id+"F4.wireOp",EDGE,"E2")])],"isStart":false})]}),makeQuery(id+"F8.opExtrude","CAP_FACE",FACE,{"disambiguationData":[OSD([subQ0])],"isStart":false})]}),"instanceName":"2"})],"blendedInto":[makeQuery(id+"F10.opPattern","COPY",FACE,{"derivedFrom":makeQuery(id+"F8.boolean.opBoolean","MERGE",FACE,{"derivedFrom":[makeQuery(id+"F5.boolean.opBoolean","MERGE",FACE,{"derivedFrom":[makeQuery(id+"F2.opExtrude","CAP_FACE",FACE,{"disambiguationData":[OSD([subQ1])],"isStart":false}),makeQuery(id+"F5.opExtrude","CAP_FACE",FACE,{"disambiguationData":[OSD([sQuery(id+"F4.wireOp",EDGE,"E2")])],"isStart":false})]}),makeQuery(id+"F8.opExtrude","CAP_FACE",FACE,{"disambiguationData":[OSD([subQ0])],"isStart":false})]}),"instanceName":"2"})]});}
            var Q13;
            Q13=makeQuery(id+"F10.opPattern","COPY",EDGE,{"derivedFrom":makeQuery(id+"F8.opExtrude","CAP_EDGE",EDGE,{"disambiguationData":[OSD([sQuery(id+"F7.wireOp",EDGE,"E4")])],"isStart":false}),"instanceName":"1"});
            var Q14;
            {var subQ0=sQuery(id+"F7.wireOp",EDGE,"E4");var subQ1=sQuery(id+"F1.wireOp",EDGE,"E1");var subQ2=makeQuery(id+"F2.opExtrude","SWEPT_FACE",FACE,{"disambiguationData":[OSD([subQ1])]});Q14=makeQuery(id+"F12.opFillet","BLEND_EDGE",EDGE,{"blendedFrom":[makeQuery(id+"F11.opChamfer","BLEND_EDGE",EDGE,{"blendedFrom":[makeQuery(id+"F10.opPattern","COPY",EDGE,{"derivedFrom":makeQuery(id+"F8.boolean.opBoolean","INTERSECT",EDGE,{"disambiguationData":[OD(1.0)],"derivedFrom":[subQ2,makeQuery(id+"F8.opExtrude","SWEPT_FACE",FACE,{"disambiguationData":[OSD([subQ0])]})]}),"instanceName":"1"}),makeQuery(id+"F10.opPattern","COPY",FACE,{"derivedFrom":subQ2,"instanceName":"1"})],"blendedInto":[makeQuery(id+"F10.opPattern","COPY",FACE,{"derivedFrom":subQ2,"instanceName":"1"})]}),makeQuery(id+"F10.opPattern","COPY",FACE,{"derivedFrom":makeQuery(id+"F8.boolean.opBoolean","MERGE",FACE,{"derivedFrom":[makeQuery(id+"F5.boolean.opBoolean","MERGE",FACE,{"derivedFrom":[makeQuery(id+"F2.opExtrude","CAP_FACE",FACE,{"disambiguationData":[OSD([subQ1])],"isStart":false}),makeQuery(id+"F5.opExtrude","CAP_FACE",FACE,{"disambiguationData":[OSD([sQuery(id+"F4.wireOp",EDGE,"E2")])],"isStart":false})]}),makeQuery(id+"F8.opExtrude","CAP_FACE",FACE,{"disambiguationData":[OSD([subQ0])],"isStart":false})]}),"instanceName":"1"})],"blendedInto":[makeQuery(id+"F10.opPattern","COPY",FACE,{"derivedFrom":makeQuery(id+"F8.boolean.opBoolean","MERGE",FACE,{"derivedFrom":[makeQuery(id+"F5.boolean.opBoolean","MERGE",FACE,{"derivedFrom":[makeQuery(id+"F2.opExtrude","CAP_FACE",FACE,{"disambiguationData":[OSD([subQ1])],"isStart":false}),makeQuery(id+"F5.opExtrude","CAP_FACE",FACE,{"disambiguationData":[OSD([sQuery(id+"F4.wireOp",EDGE,"E2")])],"isStart":false})]}),makeQuery(id+"F8.opExtrude","CAP_FACE",FACE,{"disambiguationData":[OSD([subQ0])],"isStart":false})]}),"instanceName":"1"})]});}
            fillet(context, id + "F14", {"entities" : qUnion([Q0, Q1, Q2, Q3, Q4, Q5, Q6, Q7, Q8, Q9, Q10, Q11, Q12, Q13, Q14]), "radius" : 3.5 * mm, "tangentPropagation" : true, "allowEdgeOverflow" : false});
        }
        {
            var Q0;
            {var subQ0=sQuery(id+"F7.wireOp",EDGE,"E4");var subQ1=sQuery(id+"F1.wireOp",EDGE,"E1");var subQ2=makeQuery(id+"F8.opExtrude","SWEPT_FACE",FACE,{"disambiguationData":[OSD([subQ0])]});Q0=makeQuery(id+"F13.opFillet","BLEND_EDGE",EDGE,{"blendedFrom":[makeQuery(id+"F11.opChamfer","BLEND_EDGE",EDGE,{"blendedFrom":[makeQuery(id+"F10.opPattern","COPY",EDGE,{"derivedFrom":makeQuery(id+"F8.boolean.opBoolean","INTERSECT",EDGE,{"disambiguationData":[OD(0.0)],"derivedFrom":[makeQuery(id+"F2.opExtrude","SWEPT_FACE",FACE,{"disambiguationData":[OSD([subQ1])]}),subQ2]}),"instanceName":"1"}),makeQuery(id+"F10.opPattern","COPY",FACE,{"derivedFrom":subQ2,"instanceName":"1"})],"blendedInto":[makeQuery(id+"F10.opPattern","COPY",FACE,{"derivedFrom":subQ2,"instanceName":"1"})]}),makeQuery(id+"F10.opPattern","COPY",FACE,{"derivedFrom":makeQuery(id+"F8.boolean.opBoolean","MERGE",FACE,{"derivedFrom":[makeQuery(id+"F5.boolean.opBoolean","MERGE",FACE,{"derivedFrom":[makeQuery(id+"F2.opExtrude","CAP_FACE",FACE,{"disambiguationData":[OSD([subQ1])],"isStart":true}),makeQuery(id+"F5.opExtrude","CAP_FACE",FACE,{"disambiguationData":[OSD([sQuery(id+"F4.wireOp",EDGE,"E2")])],"isStart":true})]}),makeQuery(id+"F8.opExtrude","CAP_FACE",FACE,{"disambiguationData":[OSD([subQ0])],"isStart":true})]}),"instanceName":"1"})],"blendedInto":[makeQuery(id+"F10.opPattern","COPY",FACE,{"derivedFrom":makeQuery(id+"F8.boolean.opBoolean","MERGE",FACE,{"derivedFrom":[makeQuery(id+"F5.boolean.opBoolean","MERGE",FACE,{"derivedFrom":[makeQuery(id+"F2.opExtrude","CAP_FACE",FACE,{"disambiguationData":[OSD([subQ1])],"isStart":true}),makeQuery(id+"F5.opExtrude","CAP_FACE",FACE,{"disambiguationData":[OSD([sQuery(id+"F4.wireOp",EDGE,"E2")])],"isStart":true})]}),makeQuery(id+"F8.opExtrude","CAP_FACE",FACE,{"disambiguationData":[OSD([subQ0])],"isStart":true})]}),"instanceName":"1"})]});}
            var Q1;
            Q1=makeQuery(id+"F8.opExtrude","CAP_EDGE",EDGE,{"disambiguationData":[OSD([sQuery(id+"F7.wireOp",EDGE,"E4")])],"isStart":true});
            var Q2;
            {var subQ0=sQuery(id+"F7.wireOp",EDGE,"E4");var subQ1=sQuery(id+"F1.wireOp",EDGE,"E1");var subQ2=makeQuery(id+"F8.opExtrude","SWEPT_FACE",FACE,{"disambiguationData":[OSD([subQ0])]});Q2=makeQuery(id+"F13.opFillet","BLEND_EDGE",EDGE,{"blendedFrom":[makeQuery(id+"F11.opChamfer","BLEND_EDGE",EDGE,{"blendedFrom":[makeQuery(id+"F10.opPattern","COPY",EDGE,{"derivedFrom":makeQuery(id+"F8.boolean.opBoolean","INTERSECT",EDGE,{"disambiguationData":[OD(1.0)],"derivedFrom":[makeQuery(id+"F2.opExtrude","SWEPT_FACE",FACE,{"disambiguationData":[OSD([subQ1])]}),subQ2]}),"instanceName":"2"}),makeQuery(id+"F10.opPattern","COPY",FACE,{"derivedFrom":subQ2,"instanceName":"2"})],"blendedInto":[makeQuery(id+"F10.opPattern","COPY",FACE,{"derivedFrom":subQ2,"instanceName":"2"})]}),makeQuery(id+"F10.opPattern","COPY",FACE,{"derivedFrom":makeQuery(id+"F8.boolean.opBoolean","MERGE",FACE,{"derivedFrom":[makeQuery(id+"F5.boolean.opBoolean","MERGE",FACE,{"derivedFrom":[makeQuery(id+"F2.opExtrude","CAP_FACE",FACE,{"disambiguationData":[OSD([subQ1])],"isStart":true}),makeQuery(id+"F5.opExtrude","CAP_FACE",FACE,{"disambiguationData":[OSD([sQuery(id+"F4.wireOp",EDGE,"E2")])],"isStart":true})]}),makeQuery(id+"F8.opExtrude","CAP_FACE",FACE,{"disambiguationData":[OSD([subQ0])],"isStart":true})]}),"instanceName":"2"})],"blendedInto":[makeQuery(id+"F10.opPattern","COPY",FACE,{"derivedFrom":makeQuery(id+"F8.boolean.opBoolean","MERGE",FACE,{"derivedFrom":[makeQuery(id+"F5.boolean.opBoolean","MERGE",FACE,{"derivedFrom":[makeQuery(id+"F2.opExtrude","CAP_FACE",FACE,{"disambiguationData":[OSD([subQ1])],"isStart":true}),makeQuery(id+"F5.opExtrude","CAP_FACE",FACE,{"disambiguationData":[OSD([sQuery(id+"F4.wireOp",EDGE,"E2")])],"isStart":true})]}),makeQuery(id+"F8.opExtrude","CAP_FACE",FACE,{"disambiguationData":[OSD([subQ0])],"isStart":true})]}),"instanceName":"2"})]});}
            var Q3;
            Q3=makeQuery(id+"F10.opPattern","COPY",EDGE,{"derivedFrom":makeQuery(id+"F8.opExtrude","CAP_EDGE",EDGE,{"disambiguationData":[OSD([sQuery(id+"F7.wireOp",EDGE,"E4")])],"isStart":true}),"instanceName":"2"});
            var Q4;
            {var subQ0=sQuery(id+"F7.wireOp",EDGE,"E4");var subQ1=sQuery(id+"F1.wireOp",EDGE,"E1");var subQ2=makeQuery(id+"F8.opExtrude","SWEPT_FACE",FACE,{"disambiguationData":[OSD([subQ0])]});Q4=makeQuery(id+"F13.opFillet","BLEND_EDGE",EDGE,{"blendedFrom":[makeQuery(id+"F11.opChamfer","BLEND_EDGE",EDGE,{"blendedFrom":[makeQuery(id+"F10.opPattern","COPY",EDGE,{"derivedFrom":makeQuery(id+"F8.boolean.opBoolean","INTERSECT",EDGE,{"disambiguationData":[OD(0.0)],"derivedFrom":[makeQuery(id+"F2.opExtrude","SWEPT_FACE",FACE,{"disambiguationData":[OSD([subQ1])]}),subQ2]}),"instanceName":"2"}),makeQuery(id+"F10.opPattern","COPY",FACE,{"derivedFrom":subQ2,"instanceName":"2"})],"blendedInto":[makeQuery(id+"F10.opPattern","COPY",FACE,{"derivedFrom":subQ2,"instanceName":"2"})]}),makeQuery(id+"F10.opPattern","COPY",FACE,{"derivedFrom":makeQuery(id+"F8.boolean.opBoolean","MERGE",FACE,{"derivedFrom":[makeQuery(id+"F5.boolean.opBoolean","MERGE",FACE,{"derivedFrom":[makeQuery(id+"F2.opExtrude","CAP_FACE",FACE,{"disambiguationData":[OSD([subQ1])],"isStart":true}),makeQuery(id+"F5.opExtrude","CAP_FACE",FACE,{"disambiguationData":[OSD([sQuery(id+"F4.wireOp",EDGE,"E2")])],"isStart":true})]}),makeQuery(id+"F8.opExtrude","CAP_FACE",FACE,{"disambiguationData":[OSD([subQ0])],"isStart":true})]}),"instanceName":"2"})],"blendedInto":[makeQuery(id+"F10.opPattern","COPY",FACE,{"derivedFrom":makeQuery(id+"F8.boolean.opBoolean","MERGE",FACE,{"derivedFrom":[makeQuery(id+"F5.boolean.opBoolean","MERGE",FACE,{"derivedFrom":[makeQuery(id+"F2.opExtrude","CAP_FACE",FACE,{"disambiguationData":[OSD([subQ1])],"isStart":true}),makeQuery(id+"F5.opExtrude","CAP_FACE",FACE,{"disambiguationData":[OSD([sQuery(id+"F4.wireOp",EDGE,"E2")])],"isStart":true})]}),makeQuery(id+"F8.opExtrude","CAP_FACE",FACE,{"disambiguationData":[OSD([subQ0])],"isStart":true})]}),"instanceName":"2"})]});}
            var Q5;
            {var subQ0=sQuery(id+"F7.wireOp",EDGE,"E4");var subQ1=sQuery(id+"F1.wireOp",EDGE,"E1");var subQ2=makeQuery(id+"F2.opExtrude","SWEPT_FACE",FACE,{"disambiguationData":[OSD([subQ1])]});Q5=makeQuery(id+"F12.opFillet","BLEND_EDGE",EDGE,{"blendedFrom":[makeQuery(id+"F11.opChamfer","BLEND_EDGE",EDGE,{"blendedFrom":[makeQuery(id+"F10.opPattern","COPY",EDGE,{"derivedFrom":makeQuery(id+"F8.boolean.opBoolean","INTERSECT",EDGE,{"disambiguationData":[OD(1.0)],"derivedFrom":[subQ2,makeQuery(id+"F8.opExtrude","SWEPT_FACE",FACE,{"disambiguationData":[OSD([subQ0])]})]}),"instanceName":"1"}),makeQuery(id+"F10.opPattern","COPY",FACE,{"derivedFrom":subQ2,"instanceName":"1"})],"blendedInto":[makeQuery(id+"F10.opPattern","COPY",FACE,{"derivedFrom":subQ2,"instanceName":"1"})]}),makeQuery(id+"F10.opPattern","COPY",FACE,{"derivedFrom":makeQuery(id+"F8.boolean.opBoolean","MERGE",FACE,{"derivedFrom":[makeQuery(id+"F5.boolean.opBoolean","MERGE",FACE,{"derivedFrom":[makeQuery(id+"F2.opExtrude","CAP_FACE",FACE,{"disambiguationData":[OSD([subQ1])],"isStart":true}),makeQuery(id+"F5.opExtrude","CAP_FACE",FACE,{"disambiguationData":[OSD([sQuery(id+"F4.wireOp",EDGE,"E2")])],"isStart":true})]}),makeQuery(id+"F8.opExtrude","CAP_FACE",FACE,{"disambiguationData":[OSD([subQ0])],"isStart":true})]}),"instanceName":"1"})],"blendedInto":[makeQuery(id+"F10.opPattern","COPY",FACE,{"derivedFrom":makeQuery(id+"F8.boolean.opBoolean","MERGE",FACE,{"derivedFrom":[makeQuery(id+"F5.boolean.opBoolean","MERGE",FACE,{"derivedFrom":[makeQuery(id+"F2.opExtrude","CAP_FACE",FACE,{"disambiguationData":[OSD([subQ1])],"isStart":true}),makeQuery(id+"F5.opExtrude","CAP_FACE",FACE,{"disambiguationData":[OSD([sQuery(id+"F4.wireOp",EDGE,"E2")])],"isStart":true})]}),makeQuery(id+"F8.opExtrude","CAP_FACE",FACE,{"disambiguationData":[OSD([subQ0])],"isStart":true})]}),"instanceName":"1"})]});}
            var Q6;
            {var subQ0=sQuery(id+"F7.wireOp",EDGE,"E4");var subQ1=sQuery(id+"F1.wireOp",EDGE,"E1");var subQ2=makeQuery(id+"F2.opExtrude","SWEPT_FACE",FACE,{"disambiguationData":[OSD([subQ1])]});Q6=makeQuery(id+"F12.opFillet","BLEND_EDGE",EDGE,{"blendedFrom":[makeQuery(id+"F11.opChamfer","BLEND_EDGE",EDGE,{"blendedFrom":[makeQuery(id+"F10.opPattern","COPY",EDGE,{"derivedFrom":makeQuery(id+"F8.boolean.opBoolean","INTERSECT",EDGE,{"disambiguationData":[OD(0.0)],"derivedFrom":[subQ2,makeQuery(id+"F8.opExtrude","SWEPT_FACE",FACE,{"disambiguationData":[OSD([subQ0])]})]}),"instanceName":"2"}),makeQuery(id+"F10.opPattern","COPY",FACE,{"derivedFrom":subQ2,"instanceName":"2"})],"blendedInto":[makeQuery(id+"F10.opPattern","COPY",FACE,{"derivedFrom":subQ2,"instanceName":"2"})]}),makeQuery(id+"F10.opPattern","COPY",FACE,{"derivedFrom":makeQuery(id+"F8.boolean.opBoolean","MERGE",FACE,{"derivedFrom":[makeQuery(id+"F5.boolean.opBoolean","MERGE",FACE,{"derivedFrom":[makeQuery(id+"F2.opExtrude","CAP_FACE",FACE,{"disambiguationData":[OSD([subQ1])],"isStart":true}),makeQuery(id+"F5.opExtrude","CAP_FACE",FACE,{"disambiguationData":[OSD([sQuery(id+"F4.wireOp",EDGE,"E2")])],"isStart":true})]}),makeQuery(id+"F8.opExtrude","CAP_FACE",FACE,{"disambiguationData":[OSD([subQ0])],"isStart":true})]}),"instanceName":"2"})],"blendedInto":[makeQuery(id+"F10.opPattern","COPY",FACE,{"derivedFrom":makeQuery(id+"F8.boolean.opBoolean","MERGE",FACE,{"derivedFrom":[makeQuery(id+"F5.boolean.opBoolean","MERGE",FACE,{"derivedFrom":[makeQuery(id+"F2.opExtrude","CAP_FACE",FACE,{"disambiguationData":[OSD([subQ1])],"isStart":true}),makeQuery(id+"F5.opExtrude","CAP_FACE",FACE,{"disambiguationData":[OSD([sQuery(id+"F4.wireOp",EDGE,"E2")])],"isStart":true})]}),makeQuery(id+"F8.opExtrude","CAP_FACE",FACE,{"disambiguationData":[OSD([subQ0])],"isStart":true})]}),"instanceName":"2"})]});}
            var Q7;
            {var subQ0=sQuery(id+"F7.wireOp",EDGE,"E4");var subQ1=sQuery(id+"F1.wireOp",EDGE,"E1");var subQ2=makeQuery(id+"F2.opExtrude","SWEPT_FACE",FACE,{"disambiguationData":[OSD([subQ1])]});Q7=makeQuery(id+"F12.opFillet","BLEND_EDGE",EDGE,{"blendedFrom":[makeQuery(id+"F11.opChamfer","BLEND_EDGE",EDGE,{"blendedFrom":[makeQuery(id+"F10.opPattern","COPY",EDGE,{"derivedFrom":makeQuery(id+"F8.boolean.opBoolean","INTERSECT",EDGE,{"disambiguationData":[OD(0.0)],"derivedFrom":[subQ2,makeQuery(id+"F8.opExtrude","SWEPT_FACE",FACE,{"disambiguationData":[OSD([subQ0])]})]}),"instanceName":"1"}),makeQuery(id+"F10.opPattern","COPY",FACE,{"derivedFrom":subQ2,"instanceName":"1"})],"blendedInto":[makeQuery(id+"F10.opPattern","COPY",FACE,{"derivedFrom":subQ2,"instanceName":"1"})]}),makeQuery(id+"F10.opPattern","COPY",FACE,{"derivedFrom":makeQuery(id+"F8.boolean.opBoolean","MERGE",FACE,{"derivedFrom":[makeQuery(id+"F5.boolean.opBoolean","MERGE",FACE,{"derivedFrom":[makeQuery(id+"F2.opExtrude","CAP_FACE",FACE,{"disambiguationData":[OSD([subQ1])],"isStart":true}),makeQuery(id+"F5.opExtrude","CAP_FACE",FACE,{"disambiguationData":[OSD([sQuery(id+"F4.wireOp",EDGE,"E2")])],"isStart":true})]}),makeQuery(id+"F8.opExtrude","CAP_FACE",FACE,{"disambiguationData":[OSD([subQ0])],"isStart":true})]}),"instanceName":"1"})],"blendedInto":[makeQuery(id+"F10.opPattern","COPY",FACE,{"derivedFrom":makeQuery(id+"F8.boolean.opBoolean","MERGE",FACE,{"derivedFrom":[makeQuery(id+"F5.boolean.opBoolean","MERGE",FACE,{"derivedFrom":[makeQuery(id+"F2.opExtrude","CAP_FACE",FACE,{"disambiguationData":[OSD([subQ1])],"isStart":true}),makeQuery(id+"F5.opExtrude","CAP_FACE",FACE,{"disambiguationData":[OSD([sQuery(id+"F4.wireOp",EDGE,"E2")])],"isStart":true})]}),makeQuery(id+"F8.opExtrude","CAP_FACE",FACE,{"disambiguationData":[OSD([subQ0])],"isStart":true})]}),"instanceName":"1"})]});}
            var Q8;
            {var subQ0=sQuery(id+"F7.wireOp",EDGE,"E4");var subQ1=sQuery(id+"F1.wireOp",EDGE,"E1");var subQ2=makeQuery(id+"F2.opExtrude","SWEPT_FACE",FACE,{"disambiguationData":[OSD([subQ1])]});Q8=makeQuery(id+"F12.opFillet","BLEND_EDGE",EDGE,{"blendedFrom":[makeQuery(id+"F11.opChamfer","BLEND_EDGE",EDGE,{"blendedFrom":[makeQuery(id+"F8.boolean.opBoolean","INTERSECT",EDGE,{"disambiguationData":[OD(1.0)],"derivedFrom":[subQ2,makeQuery(id+"F8.opExtrude","SWEPT_FACE",FACE,{"disambiguationData":[OSD([subQ0])]})]}),subQ2],"blendedInto":[subQ2]}),makeQuery(id+"F8.boolean.opBoolean","MERGE",FACE,{"derivedFrom":[makeQuery(id+"F5.boolean.opBoolean","MERGE",FACE,{"derivedFrom":[makeQuery(id+"F2.opExtrude","CAP_FACE",FACE,{"disambiguationData":[OSD([subQ1])],"isStart":true}),makeQuery(id+"F5.opExtrude","CAP_FACE",FACE,{"disambiguationData":[OSD([sQuery(id+"F4.wireOp",EDGE,"E2")])],"isStart":true})]}),makeQuery(id+"F8.opExtrude","CAP_FACE",FACE,{"disambiguationData":[OSD([subQ0])],"isStart":true})]})],"blendedInto":[makeQuery(id+"F8.boolean.opBoolean","MERGE",FACE,{"derivedFrom":[makeQuery(id+"F5.boolean.opBoolean","MERGE",FACE,{"derivedFrom":[makeQuery(id+"F2.opExtrude","CAP_FACE",FACE,{"disambiguationData":[OSD([subQ1])],"isStart":true}),makeQuery(id+"F5.opExtrude","CAP_FACE",FACE,{"disambiguationData":[OSD([sQuery(id+"F4.wireOp",EDGE,"E2")])],"isStart":true})]}),makeQuery(id+"F8.opExtrude","CAP_FACE",FACE,{"disambiguationData":[OSD([subQ0])],"isStart":true})]})]});}
            var Q9;
            {var subQ0=sQuery(id+"F7.wireOp",EDGE,"E4");var subQ1=sQuery(id+"F1.wireOp",EDGE,"E1");var subQ2=makeQuery(id+"F2.opExtrude","SWEPT_FACE",FACE,{"disambiguationData":[OSD([subQ1])]});Q9=makeQuery(id+"F12.opFillet","BLEND_EDGE",EDGE,{"blendedFrom":[makeQuery(id+"F11.opChamfer","BLEND_EDGE",EDGE,{"blendedFrom":[makeQuery(id+"F10.opPattern","COPY",EDGE,{"derivedFrom":makeQuery(id+"F8.boolean.opBoolean","INTERSECT",EDGE,{"disambiguationData":[OD(1.0)],"derivedFrom":[subQ2,makeQuery(id+"F8.opExtrude","SWEPT_FACE",FACE,{"disambiguationData":[OSD([subQ0])]})]}),"instanceName":"2"}),makeQuery(id+"F10.opPattern","COPY",FACE,{"derivedFrom":subQ2,"instanceName":"2"})],"blendedInto":[makeQuery(id+"F10.opPattern","COPY",FACE,{"derivedFrom":subQ2,"instanceName":"2"})]}),makeQuery(id+"F10.opPattern","COPY",FACE,{"derivedFrom":makeQuery(id+"F8.boolean.opBoolean","MERGE",FACE,{"derivedFrom":[makeQuery(id+"F5.boolean.opBoolean","MERGE",FACE,{"derivedFrom":[makeQuery(id+"F2.opExtrude","CAP_FACE",FACE,{"disambiguationData":[OSD([subQ1])],"isStart":true}),makeQuery(id+"F5.opExtrude","CAP_FACE",FACE,{"disambiguationData":[OSD([sQuery(id+"F4.wireOp",EDGE,"E2")])],"isStart":true})]}),makeQuery(id+"F8.opExtrude","CAP_FACE",FACE,{"disambiguationData":[OSD([subQ0])],"isStart":true})]}),"instanceName":"2"})],"blendedInto":[makeQuery(id+"F10.opPattern","COPY",FACE,{"derivedFrom":makeQuery(id+"F8.boolean.opBoolean","MERGE",FACE,{"derivedFrom":[makeQuery(id+"F5.boolean.opBoolean","MERGE",FACE,{"derivedFrom":[makeQuery(id+"F2.opExtrude","CAP_FACE",FACE,{"disambiguationData":[OSD([subQ1])],"isStart":true}),makeQuery(id+"F5.opExtrude","CAP_FACE",FACE,{"disambiguationData":[OSD([sQuery(id+"F4.wireOp",EDGE,"E2")])],"isStart":true})]}),makeQuery(id+"F8.opExtrude","CAP_FACE",FACE,{"disambiguationData":[OSD([subQ0])],"isStart":true})]}),"instanceName":"2"})]});}
            var Q10;
            {var subQ0=sQuery(id+"F7.wireOp",EDGE,"E4");var subQ1=sQuery(id+"F1.wireOp",EDGE,"E1");var subQ2=makeQuery(id+"F8.opExtrude","SWEPT_FACE",FACE,{"disambiguationData":[OSD([subQ0])]});Q10=makeQuery(id+"F13.opFillet","BLEND_EDGE",EDGE,{"blendedFrom":[makeQuery(id+"F11.opChamfer","BLEND_EDGE",EDGE,{"blendedFrom":[makeQuery(id+"F10.opPattern","COPY",EDGE,{"derivedFrom":makeQuery(id+"F8.boolean.opBoolean","INTERSECT",EDGE,{"disambiguationData":[OD(1.0)],"derivedFrom":[makeQuery(id+"F2.opExtrude","SWEPT_FACE",FACE,{"disambiguationData":[OSD([subQ1])]}),subQ2]}),"instanceName":"1"}),makeQuery(id+"F10.opPattern","COPY",FACE,{"derivedFrom":subQ2,"instanceName":"1"})],"blendedInto":[makeQuery(id+"F10.opPattern","COPY",FACE,{"derivedFrom":subQ2,"instanceName":"1"})]}),makeQuery(id+"F10.opPattern","COPY",FACE,{"derivedFrom":makeQuery(id+"F8.boolean.opBoolean","MERGE",FACE,{"derivedFrom":[makeQuery(id+"F5.boolean.opBoolean","MERGE",FACE,{"derivedFrom":[makeQuery(id+"F2.opExtrude","CAP_FACE",FACE,{"disambiguationData":[OSD([subQ1])],"isStart":true}),makeQuery(id+"F5.opExtrude","CAP_FACE",FACE,{"disambiguationData":[OSD([sQuery(id+"F4.wireOp",EDGE,"E2")])],"isStart":true})]}),makeQuery(id+"F8.opExtrude","CAP_FACE",FACE,{"disambiguationData":[OSD([subQ0])],"isStart":true})]}),"instanceName":"1"})],"blendedInto":[makeQuery(id+"F10.opPattern","COPY",FACE,{"derivedFrom":makeQuery(id+"F8.boolean.opBoolean","MERGE",FACE,{"derivedFrom":[makeQuery(id+"F5.boolean.opBoolean","MERGE",FACE,{"derivedFrom":[makeQuery(id+"F2.opExtrude","CAP_FACE",FACE,{"disambiguationData":[OSD([subQ1])],"isStart":true}),makeQuery(id+"F5.opExtrude","CAP_FACE",FACE,{"disambiguationData":[OSD([sQuery(id+"F4.wireOp",EDGE,"E2")])],"isStart":true})]}),makeQuery(id+"F8.opExtrude","CAP_FACE",FACE,{"disambiguationData":[OSD([subQ0])],"isStart":true})]}),"instanceName":"1"})]});}
            var Q11;
            Q11=makeQuery(id+"F10.opPattern","COPY",EDGE,{"derivedFrom":makeQuery(id+"F8.opExtrude","CAP_EDGE",EDGE,{"disambiguationData":[OSD([sQuery(id+"F7.wireOp",EDGE,"E4")])],"isStart":true}),"instanceName":"1"});
            var Q12;
            {var subQ0=sQuery(id+"F7.wireOp",EDGE,"E4");var subQ1=sQuery(id+"F1.wireOp",EDGE,"E1");var subQ2=makeQuery(id+"F8.opExtrude","SWEPT_FACE",FACE,{"disambiguationData":[OSD([subQ0])]});Q12=makeQuery(id+"F13.opFillet","BLEND_EDGE",EDGE,{"blendedFrom":[makeQuery(id+"F11.opChamfer","BLEND_EDGE",EDGE,{"blendedFrom":[makeQuery(id+"F8.boolean.opBoolean","INTERSECT",EDGE,{"disambiguationData":[OD(1.0)],"derivedFrom":[makeQuery(id+"F2.opExtrude","SWEPT_FACE",FACE,{"disambiguationData":[OSD([subQ1])]}),subQ2]}),subQ2],"blendedInto":[subQ2]}),makeQuery(id+"F8.boolean.opBoolean","MERGE",FACE,{"derivedFrom":[makeQuery(id+"F5.boolean.opBoolean","MERGE",FACE,{"derivedFrom":[makeQuery(id+"F2.opExtrude","CAP_FACE",FACE,{"disambiguationData":[OSD([subQ1])],"isStart":true}),makeQuery(id+"F5.opExtrude","CAP_FACE",FACE,{"disambiguationData":[OSD([sQuery(id+"F4.wireOp",EDGE,"E2")])],"isStart":true})]}),makeQuery(id+"F8.opExtrude","CAP_FACE",FACE,{"disambiguationData":[OSD([subQ0])],"isStart":true})]})],"blendedInto":[makeQuery(id+"F8.boolean.opBoolean","MERGE",FACE,{"derivedFrom":[makeQuery(id+"F5.boolean.opBoolean","MERGE",FACE,{"derivedFrom":[makeQuery(id+"F2.opExtrude","CAP_FACE",FACE,{"disambiguationData":[OSD([subQ1])],"isStart":true}),makeQuery(id+"F5.opExtrude","CAP_FACE",FACE,{"disambiguationData":[OSD([sQuery(id+"F4.wireOp",EDGE,"E2")])],"isStart":true})]}),makeQuery(id+"F8.opExtrude","CAP_FACE",FACE,{"disambiguationData":[OSD([subQ0])],"isStart":true})]})]});}
            fillet(context, id + "F15", {"entities" : qUnion([Q0, Q1, Q2, Q3, Q4, Q5, Q6, Q7, Q8, Q9, Q10, Q11, Q12]), "radius" : 3.5 * mm, "tangentPropagation" : true, "allowEdgeOverflow" : false});
        }
        {
            var Q0;
            Q0=makeQuery(id+"F8.boolean.opBoolean","MERGE",FACE,{"derivedFrom":[makeQuery(id+"F5.boolean.opBoolean","MERGE",FACE,{"derivedFrom":[makeQuery(id+"F2.opExtrude","CAP_FACE",FACE,{"disambiguationData":[OSD([sQuery(id+"F1.wireOp",EDGE,"E1")])],"isStart":false}),makeQuery(id+"F5.opExtrude","CAP_FACE",FACE,{"disambiguationData":[OSD([sQuery(id+"F4.wireOp",EDGE,"E2")])],"isStart":false})]}),makeQuery(id+"F8.opExtrude","CAP_FACE",FACE,{"disambiguationData":[OSD([sQuery(id+"F7.wireOp",EDGE,"E4")])],"isStart":false})]});
            var sketch = newSketch(context, id + "F16", { "sketchPlane" : qUnion([Q0])});
            skLineSegment(sketch, "E5.bottom", {"start": v(-10.53, -9.17) * mm, "end": v(-9.71, -9.17) * mm});
            skLineSegment(sketch, "E5.top", {"start": v(-10.53, -18.91) * mm, "end": v(-9.71, -18.91) * mm});
            skLineSegment(sketch, "E5.left", {"start": v(-10.53, -9.17) * mm, "end": v(-10.53, -18.91) * mm});
            skLineSegment(sketch, "E5.right", {"start": v(-9.71, -9.17) * mm, "end": v(-9.71, -18.91) * mm});
            skSolve(sketch);
        }
        {
            var Q0;
            Q0=makeQuery(id+"F16.imprint","IMPRINT",FACE,{"disambiguationData":[TD([[makeQuery(id+"F16.imprint","IMPRINT",EDGE,{"derivedFrom":sQuery(id+"F16.wireOp",EDGE,"E5.bottom")}),1.0]])]});
            var sketch = newSketch(context, id + "F17", { "sketchPlane" : qUnion([Q0])});
            skLineSegment(sketch, "E6.bottom", {"start": v(-9.7, -9.22) * mm, "end": v(-6.1, -9.22) * mm});
            skLineSegment(sketch, "E6.top", {"start": v(-9.7, -10.2) * mm, "end": v(-6.1, -10.2) * mm});
            skLineSegment(sketch, "E6.left", {"start": v(-9.7, -9.22) * mm, "end": v(-9.7, -10.2) * mm});
            skLineSegment(sketch, "E6.right", {"start": v(-6.1, -9.22) * mm, "end": v(-6.1, -10.2) * mm});
            skSolve(sketch);
        }
        {
            var Q0;
            Q0=makeQuery(id+"F17.imprint","IMPRINT",FACE,{"disambiguationData":[TD([[makeQuery(id+"F17.imprint","IMPRINT",EDGE,{"derivedFrom":sQuery(id+"F17.wireOp",EDGE,"E6.bottom")}),1.0]])]});
            var sketch = newSketch(context, id + "F18", { "sketchPlane" : qUnion([Q0])});
            skLineSegment(sketch, "E7.bottom", {"start": v(-9.67, -11.66) * mm, "end": v(-6.91, -11.66) * mm});
            skLineSegment(sketch, "E7.top", {"start": v(-9.67, -12.51) * mm, "end": v(-6.91, -12.51) * mm});
            skLineSegment(sketch, "E7.left", {"start": v(-9.67, -11.66) * mm, "end": v(-9.67, -12.51) * mm});
            skLineSegment(sketch, "E7.right", {"start": v(-6.91, -11.66) * mm, "end": v(-6.91, -12.51) * mm});
            skSolve(sketch);
        }
        {
            var Q0;
            Q0=makeQuery(id+"F16.imprint","IMPRINT",FACE,{"disambiguationData":[TD([[makeQuery(id+"F16.imprint","IMPRINT",EDGE,{"derivedFrom":sQuery(id+"F16.wireOp",EDGE,"E5.bottom")}),-1.0]])]});
            var Q1;
            Q1=makeQuery(id+"F18.imprint","IMPRINT",FACE,{"disambiguationData":[TD([[makeQuery(id+"F18.imprint","IMPRINT",EDGE,{"derivedFrom":makeQuery(id+"F17.imprint","IMPRINT",EDGE,{"derivedFrom":sQuery(id+"F17.wireOp",EDGE,"E6.bottom")})}),-1.0]])]});
            extrude(context, id + "F19", {"entities" : qUnion([Q0, Q1]), "depth" : 1 * mm, "offsetDistance" : 25 * mm});
        }
        {
            var Q0;
            Q0=makeQuery(id+"F18.imprint","IMPRINT",FACE,{"disambiguationData":[TD([[makeQuery(id+"F18.imprint","IMPRINT",EDGE,{"derivedFrom":sQuery(id+"F18.wireOp",EDGE,"E7.bottom")}),-1.0]])]});
            extrude(context, id + "F20", {"entities" : qUnion([Q0]), "depth" : 1 * mm, "offsetDistance" : 25 * mm});
        }
        {
            var Q0;
            Q0=makeQuery(id+"F10.opPattern","COPY",FACE,{"derivedFrom":makeQuery(id+"F8.boolean.opBoolean","MERGE",FACE,{"derivedFrom":[makeQuery(id+"F5.boolean.opBoolean","MERGE",FACE,{"derivedFrom":[makeQuery(id+"F2.opExtrude","CAP_FACE",FACE,{"disambiguationData":[OSD([sQuery(id+"F1.wireOp",EDGE,"E1")])],"isStart":false}),makeQuery(id+"F5.opExtrude","CAP_FACE",FACE,{"disambiguationData":[OSD([sQuery(id+"F4.wireOp",EDGE,"E2")])],"isStart":false})]}),makeQuery(id+"F8.opExtrude","CAP_FACE",FACE,{"disambiguationData":[OSD([sQuery(id+"F7.wireOp",EDGE,"E4")])],"isStart":false})]}),"instanceName":"2"});
            var sketch = newSketch(context, id + "F21", { "sketchPlane" : qUnion([Q0])});
            skLineSegment(sketch, "E8.bottom", {"start": v(11.14, 9.78) * mm, "end": v(11.97, 9.78) * mm});
            skLineSegment(sketch, "E8.top", {"start": v(11.14, 19.93) * mm, "end": v(11.97, 19.93) * mm});
            skLineSegment(sketch, "E8.left", {"start": v(11.14, 9.78) * mm, "end": v(11.14, 19.93) * mm});
            skLineSegment(sketch, "E8.right", {"start": v(11.97, 9.78) * mm, "end": v(11.97, 19.93) * mm});
            skSolve(sketch);
        }
        {
            var Q0;
            Q0=makeQuery(id+"F21.imprint","IMPRINT",FACE,{"disambiguationData":[TD([[makeQuery(id+"F21.imprint","IMPRINT",EDGE,{"derivedFrom":sQuery(id+"F21.wireOp",EDGE,"E8.bottom")}),-1.0]])]});
            var sketch = newSketch(context, id + "F22", { "sketchPlane" : qUnion([Q0])});
            skLineSegment(sketch, "E9.bottom", {"start": v(11.14, 9.8) * mm, "end": v(6.48, 9.8) * mm});
            skLineSegment(sketch, "E9.top", {"start": v(11.14, 10.96) * mm, "end": v(6.48, 10.96) * mm});
            skLineSegment(sketch, "E9.left", {"start": v(11.14, 9.8) * mm, "end": v(11.14, 10.96) * mm});
            skLineSegment(sketch, "E9.right", {"start": v(6.48, 9.8) * mm, "end": v(6.48, 10.96) * mm});
            skSolve(sketch);
        }
        {
            var Q0;
            Q0=makeQuery(id+"F21.imprint","IMPRINT",FACE,{"disambiguationData":[TD([[makeQuery(id+"F21.imprint","IMPRINT",EDGE,{"derivedFrom":sQuery(id+"F21.wireOp",EDGE,"E8.bottom")}),-1.0]])]});
            var sketch = newSketch(context, id + "F23", { "sketchPlane" : qUnion([Q0])});
            skLineSegment(sketch, "E10.bottom", {"start": v(11.13, 12.55) * mm, "end": v(8.22, 12.55) * mm});
            skLineSegment(sketch, "E10.top", {"start": v(11.13, 13.28) * mm, "end": v(8.22, 13.28) * mm});
            skLineSegment(sketch, "E10.left", {"start": v(11.13, 12.55) * mm, "end": v(11.13, 13.28) * mm});
            skLineSegment(sketch, "E10.right", {"start": v(8.22, 12.55) * mm, "end": v(8.22, 13.28) * mm});
            skSolve(sketch);
        }
        {
            var Q0;
            Q0=makeQuery(id+"F21.imprint","IMPRINT",FACE,{"disambiguationData":[TD([[makeQuery(id+"F21.imprint","IMPRINT",EDGE,{"derivedFrom":sQuery(id+"F21.wireOp",EDGE,"E8.bottom")}),1.0]])]});
            var Q1;
            Q1=makeQuery(id+"F22.imprint","IMPRINT",FACE,{"disambiguationData":[TD([[makeQuery(id+"F22.imprint","IMPRINT",EDGE,{"derivedFrom":sQuery(id+"F22.wireOp",EDGE,"E9.bottom")}),-1.0]])]});
            var Q2;
            Q2=makeQuery(id+"F23.imprint","IMPRINT",FACE,{"disambiguationData":[TD([[makeQuery(id+"F23.imprint","IMPRINT",EDGE,{"derivedFrom":sQuery(id+"F23.wireOp",EDGE,"E10.bottom")}),-1.0]])]});
            extrude(context, id + "F24", {"entities" : qUnion([Q0, Q1, Q2]), "depth" : 1 * mm, "offsetDistance" : 25 * mm});
        }
    });
